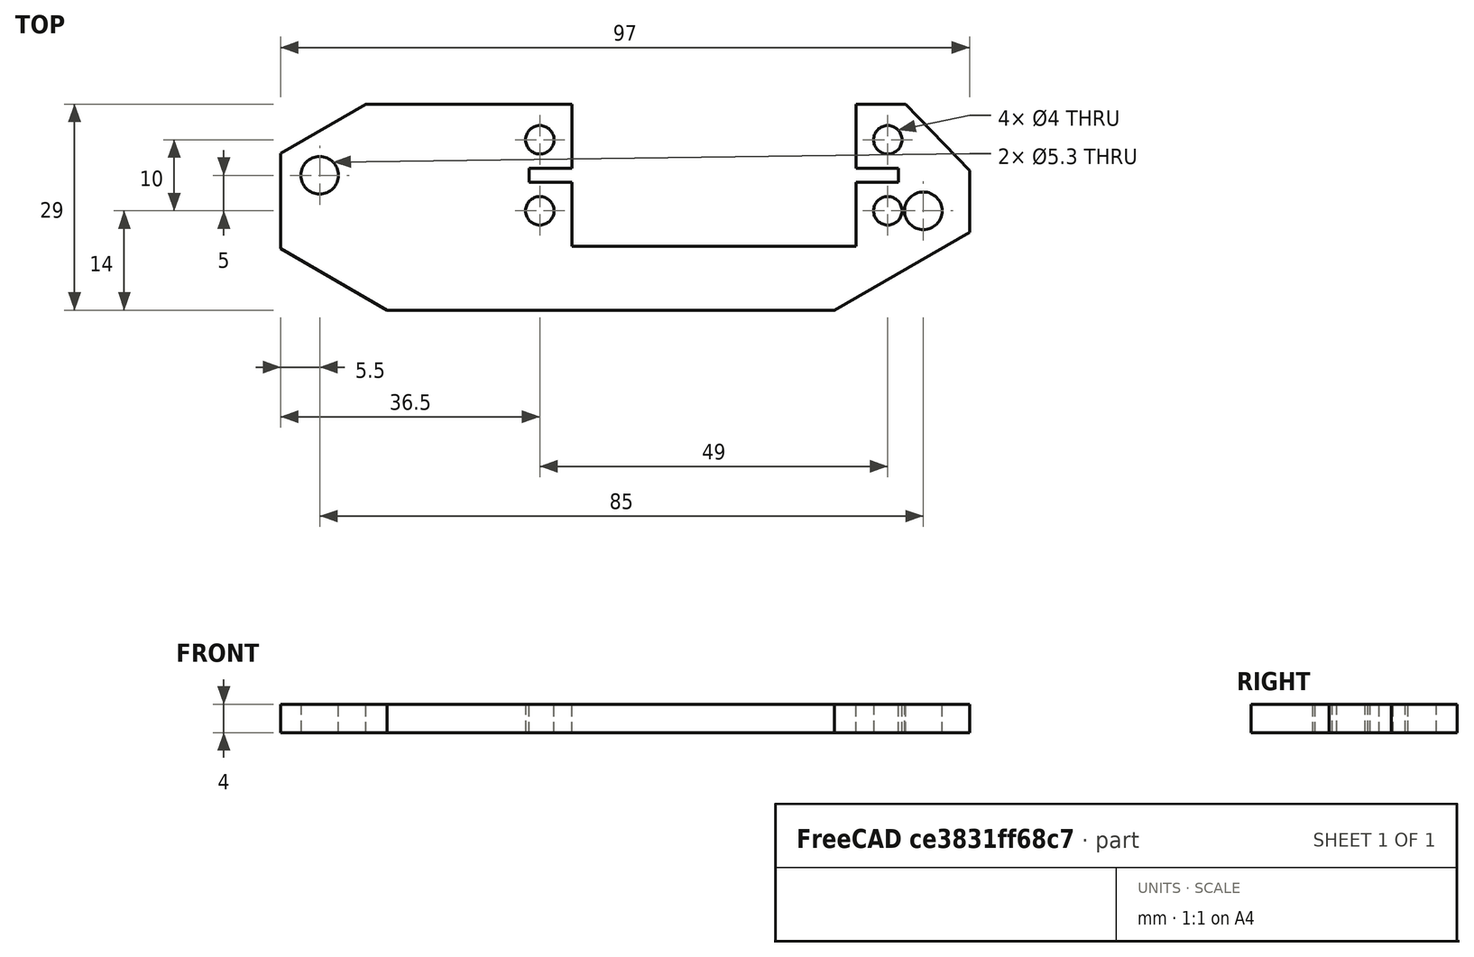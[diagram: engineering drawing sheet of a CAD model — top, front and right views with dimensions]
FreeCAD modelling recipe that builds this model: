
FCSTD DOCUMENT  (FreeCAD 0.19R24276 (Git))
Label: Servo_support_V4_long_oppozite_side
License: All rights reserved
LicenseURL: http://en.wikipedia.org/wiki/All_rights_reserved
objects: Sketcher::SketchObject×1, PartDesign::Pad×1, PartDesign::Body×1
note: 4 computed .brp shape members not serialized (recipe doc carries the construction recipe); baked Part::Feature solids carry a one-line shape summary decoded from their .brp

FEATURE [Sketcher::SketchObject] Sketch005  label="Sketch005_54x20"
  AttachmentOffset = pos=(0,0,-5) rot=(0,0,1;0rad)
  FullyConstrained = false
  MapMode = 5
  Placement = pos=(0,0,-3) rot=(0,0,1;0rad)
  sketch-geometry (41):
    g0: GeomPoint X=11 Y=0 Z=0
    g1: GeomPoint X=11 Y=0 Z=0
    g2: GeomPoint X=11 Y=0 Z=0
    g3: GeomPoint X=11 Y=0 Z=0
    g4: Circle CenterX=-13.5 CenterY=5 CenterZ=0 NormalX=0 NormalY=0 NormalZ=1 AngleXU=0 Radius=2
    g5: Circle CenterX=-13.5 CenterY=-5 CenterZ=0 NormalX=0 NormalY=0 NormalZ=1 AngleXU=0 Radius=2
    g6: LineSegment StartX=11 StartY=0 StartZ=0 EndX=11 EndY=-5 EndZ=0
    g7: Circle CenterX=35.5 CenterY=5 CenterZ=0 NormalX=0 NormalY=0 NormalZ=1 AngleXU=0 Radius=2
    g8: Circle CenterX=35.5 CenterY=-5 CenterZ=0 NormalX=0 NormalY=0 NormalZ=1 AngleXU=0 Radius=2
    g9: LineSegment StartX=11 StartY=0 StartZ=0 EndX=-13.5 EndY=0 EndZ=0
    g10: LineSegment StartX=11 StartY=0 StartZ=0 EndX=49.8748 EndY=0 EndZ=0
    g11: ArcOfCircle CenterX=-7.75 CenterY=13.4234 CenterZ=0 NormalX=0 NormalY=0 NormalZ=1 AngleXU=0 Radius=9 StartAngle=0.290352 EndAngle=2.85124
    g12: LineSegment StartX=0 StartY=0 StartZ=0 EndX=-7.75 EndY=13.4234 EndZ=0
    g13: Circle CenterX=-44.5 CenterY=0 CenterZ=0 NormalX=0 NormalY=0 NormalZ=1 AngleXU=0 Radius=2.65
    g14: LineSegment StartX=-50 StartY=-19 StartZ=0 EndX=47 EndY=-19 EndZ=0
    g15: Circle CenterX=-44.5 CenterY=0 CenterZ=0 NormalX=0 NormalY=0 NormalZ=1 AngleXU=0 Radius=5.5
    g16: LineSegment StartX=-38 StartY=10 StartZ=0 EndX=-9 EndY=10 EndZ=0
    g17: LineSegment StartX=47 StartY=0.7 StartZ=0 EndX=47 EndY=-8.03034 EndZ=0
    g18: LineSegment StartX=-9 StartY=-10 StartZ=0 EndX=31 EndY=-10 EndZ=0
    g19: LineSegment StartX=31 StartY=-10 StartZ=0 EndX=31 EndY=-1 EndZ=0
    g20: Circle CenterX=40.5 CenterY=-5 CenterZ=0 NormalX=0 NormalY=0 NormalZ=1 AngleXU=0 Radius=2.65
    g21: Circle CenterX=40.5 CenterY=-5 CenterZ=0 NormalX=0 NormalY=0 NormalZ=1 AngleXU=0 Radius=5.5
    g22: LineSegment StartX=-9 StartY=-10 StartZ=0 EndX=-9 EndY=-1 EndZ=0
    g23: LineSegment StartX=-38 StartY=10 StartZ=0 EndX=-50 EndY=3.07 EndZ=0
    g24: LineSegment StartX=-50 StartY=3.07 StartZ=0 EndX=-50 EndY=-19 EndZ=0
    g25: LineSegment StartX=-50 StartY=-10.3397 StartZ=0 EndX=-35 EndY=-19 EndZ=0
    g26: LineSegment StartX=28 StartY=-19 StartZ=0 EndX=47 EndY=-8.03034 EndZ=0
    g27: LineSegment StartX=-50 StartY=3.07 StartZ=0 EndX=-50 EndY=-10.3397 EndZ=0
    g28: LineSegment StartX=-35 StartY=-19 StartZ=0 EndX=28 EndY=-19 EndZ=0
    g29: LineSegment StartX=-15 StartY=1 StartZ=0 EndX=-9 EndY=1 EndZ=0
    g30: LineSegment StartX=-9 StartY=-1 StartZ=0 EndX=-15 EndY=-1 EndZ=0
    g31: LineSegment StartX=-15 StartY=-1 StartZ=0 EndX=-15 EndY=1 EndZ=0
    g32: LineSegment StartX=31 StartY=1 StartZ=0 EndX=37 EndY=1 EndZ=0
    g33: LineSegment StartX=37 StartY=1 StartZ=0 EndX=37 EndY=-1 EndZ=0
    g34: LineSegment StartX=37 StartY=-1 StartZ=0 EndX=31 EndY=-1 EndZ=0
    g35: LineSegment StartX=7.12713 StartY=-1 StartZ=0 EndX=7.12713 EndY=1 EndZ=0
    g36: LineSegment StartX=-13.5 StartY=0 StartZ=0 EndX=-15 EndY=0 EndZ=0
    g37: LineSegment StartX=-9 StartY=1 StartZ=0 EndX=-9 EndY=10 EndZ=0
    g38: LineSegment StartX=31 StartY=1 StartZ=0 EndX=31 EndY=10 EndZ=0
    g39: LineSegment StartX=31 StartY=10 StartZ=0 EndX=38 EndY=10 EndZ=0
    g40: LineSegment StartX=47 StartY=0.7 StartZ=0 EndX=38 EndY=10 EndZ=0
  constraints (105):
    c: Coincident(g1,g0)
    c: Coincident(g3,g2)
    c: Coincident(g2,g0)
    c: Vertical(g5,g4)
    c: Coincident(g6,g0)
    c: Vertical(g6)
    c: Equal(g8,g7)
    c: Equal(g7,g5)
    c: Equal(g5,g4)
    c: Diameter(g8) = 4
    c: Vertical(g7,g8)
    c: Horizontal(g5,g8)
    c: Horizontal(g4,g7)
    c: Coincident(g9,g0)
    c: Horizontal(g9)
    c: Symmetric(g5,g4,g9)
    c: Coincident(g10,g0)
    c: Horizontal(g10)
    c: Symmetric(g5,g8,g6)
    c: DistanceY(g8,g7) = 10
    c: DistanceX(g5,g8) = 49
    c: Horizontal(g0,g-1)
    c: Diameter(g11) = 18
    c: Coincident(g12,g-1)
    c: Coincident(g12,g11)
    c: Angle(g10,g12) = 2.0944
    c: Distance(g11,g-1) = 15.5
    c: Diameter(g13) = 5.3
    c: Horizontal(g14)
    c: Coincident(g15,g13)
    c: Diameter(g15) = 11
    c: Horizontal(g16)
    c: DistanceY(g18,g0) = 10
    c: Horizontal(g18)
    c: Coincident(g19,g18)
    c: PointOnObject(g38,g16)
    c: Vertical(g19)
    c: DistanceX(g-1,g8) = 35.5
    c: DistanceX(g18,g18) = 40
    c: DistanceY(g14,g10) = 19
    c: Horizontal(g13,g0)
    c: DistanceX(g13,g-1) = 44.5
    c: Diameter(g20) = 5.3
    c: DistanceY(g20,g10) = 5
    c: DistanceX(g-1,g20) = 40.5
    c: DistanceX(g14,g-1) = 50
    c: DistanceX(g14,g14) = 97
    c: Vertical(g17)
    c: Coincident(g21,g20)
    c: Equal(g15,g21)
    c: DistanceY(g13,g16) = 10
    c: DistanceX(g23,g16) = 12
    c: DistanceY(g23,g16) = 6.93
    c: Coincident(g22,g18)
    c: Coincident(g37,g16)
    c: Vertical(g22)
    c: DistanceX(g-1,g18) = 31
    c: Coincident(g23,g16)
    c: Coincident(g24,g23)
    c: Coincident(g24,g14)
    c: DistanceY(g14,g17) = 19.7
    c: Angle(g26,g14) = 2.61799
    c: Angle(g14,g25) = 2.61799
    c: PointOnObject(g26,g14)
    c: PointOnObject(g25,g14)
    c: DistanceX(g26,g17) = 19
    c: Coincident(g17,g26)
    c: DistanceX(g24,g25) = 15
    c: PointOnObject(g25,g24)
    c: Coincident(g27,g23)
    c: Coincident(g27,g25)
    c: Coincident(g28,g25)
    c: Coincident(g28,g26)
    c: DistanceX(g25,g17) = 97
    c: Coincident(g30,g31)
    c: Coincident(g31,g29)
    c: Horizontal(g29)
    c: Horizontal(g30)
    c: Vertical(g31)
    c: Coincident(g32,g33)
    c: Coincident(g33,g34)
    c: Horizontal(g32)
    c: Horizontal(g34)
    c: Vertical(g33)
    c: Vertical(g35)
    c: DistanceX(g29,g16) = 6
    c: Coincident(g36,g9)
    c: Horizontal(g36)
    c: Symmetric(g29,g30,g36)
    c: Coincident(g37,g29)
    c: Tangent(g22,g37)
    c: Coincident(g22,g30)
    c: DistanceY(g22,g37) = 2
    c: DistanceX(g38,g32) = 6
    c: Coincident(g38,g32)
    c: Tangent(g19,g38)
    c: Coincident(g19,g34)
    c: Horizontal(g29,g38)
    c: Horizontal(g19,g22)
    c: DistanceX(g16,g16) = 29
    c: Coincident(g39,g38)
    c: Horizontal(g39)
    c: Coincident(g40,g17)
    c: Coincident(g40,g39)
    c: DistanceX(g39,g39) = 7
FEATURE [PartDesign::Pad] Pad
  Direction = (1,1,1)
  Length = 4
  Length2 = 100
  Placement = pos=(0,0,-3) rot=(0,0,1;0rad)
  Profile = -> Sketch005
  Type = 0
FEATURE [PartDesign::Body] Body
  Group = -> [Sketch005,Pad]
  Origin = -> Origin
  Tip = -> Pad
